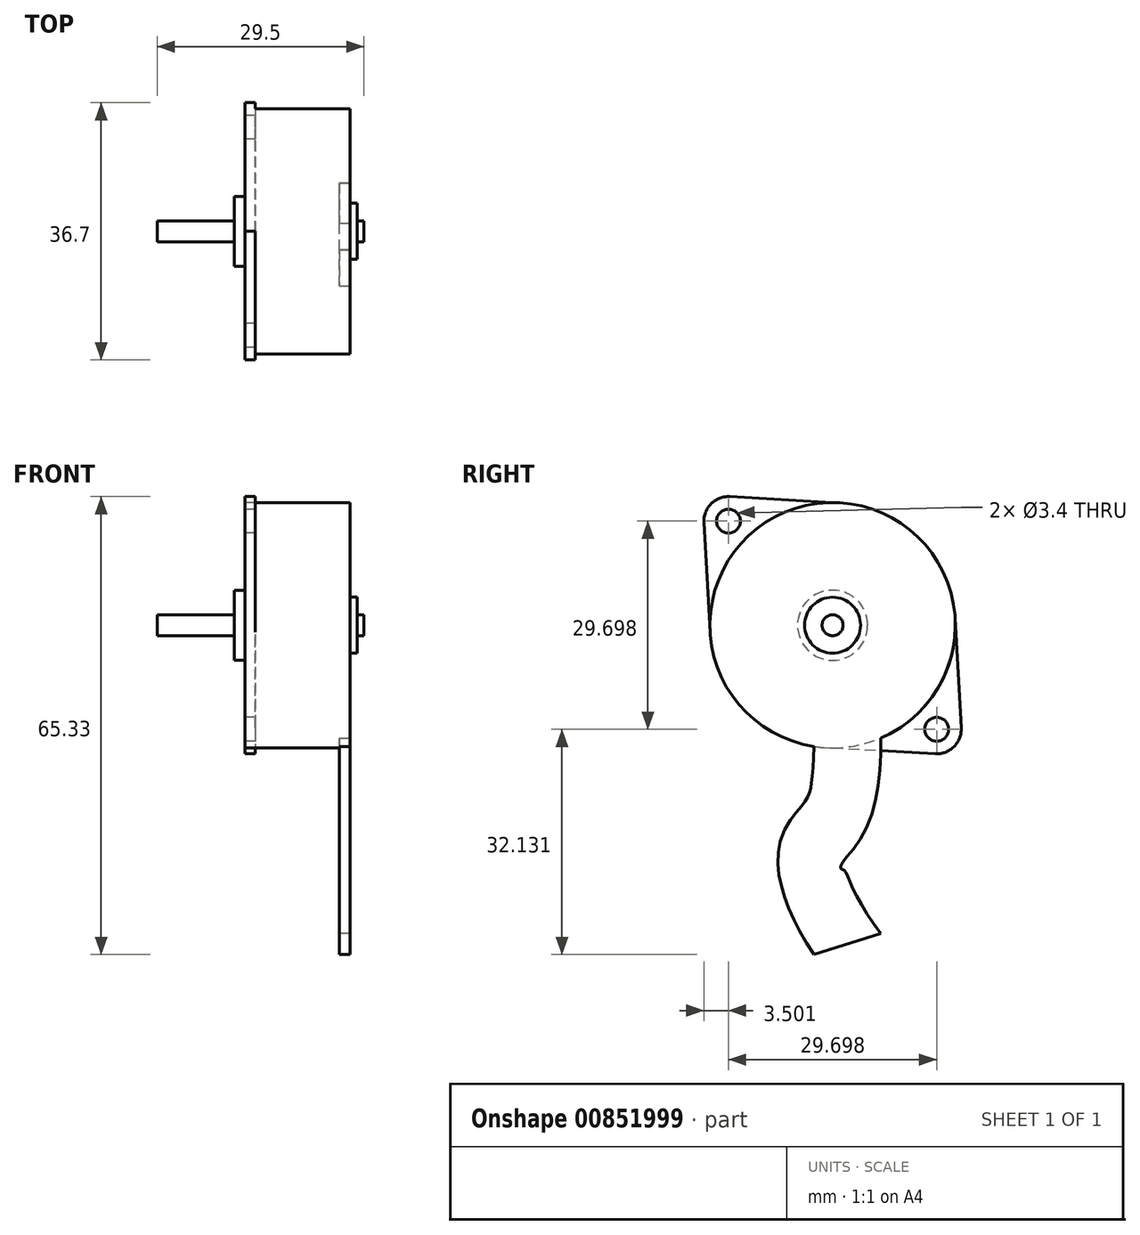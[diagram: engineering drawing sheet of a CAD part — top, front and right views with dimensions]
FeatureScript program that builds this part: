
annotation { "Feature Type Name" : "Feature", "Feature Type Description" : "" }
export const myFeature = defineFeature(function(context is Context, id is Id, definition is map)
    precondition{}
    {
        {
            var Q0;
            Q0=qCreatedBy(makeId("Front.planeOp"),FACE);
            var sketch = newSketch(context, id + "F0", { "sketchPlane" : qUnion([Q0])});
            skLineSegment(sketch, "E0", {"start": v(0, 17.5) * mm, "end": v(15, 17.5) * mm});
            skLineSegment(sketch, "E1", {"start": v(17, 0) * mm, "end": v(0, 0) * mm});
            skLineSegment(sketch, "E2", {"start": v(15, 4) * mm, "end": v(16, 4) * mm});
            skLineSegment(sketch, "E3", {"start": v(16, 4) * mm, "end": v(16, 1.5) * mm});
            skLineSegment(sketch, "E4", {"start": v(16, 1.5) * mm, "end": v(17, 1.5) * mm});
            skLineSegment(sketch, "E5", {"start": v(17, 1.5) * mm, "end": v(17, 0) * mm});
            skLineSegment(sketch, "E6", {"start": v(15, 17.5) * mm, "end": v(15, 4) * mm});
            skLineSegment(sketch, "E7", {"start": v(0, 17.5) * mm, "end": v(0, 5) * mm});
            skLineSegment(sketch, "E8", {"start": v(0, 5) * mm, "end": v(-1.5, 5) * mm});
            skLineSegment(sketch, "E9", {"start": v(-1.5, 5) * mm, "end": v(-1.5, 1.5) * mm});
            skLineSegment(sketch, "E10", {"start": v(-1.5, 1.5) * mm, "end": v(-12.5, 1.5) * mm});
            skLineSegment(sketch, "E11", {"start": v(-12.5, 1.5) * mm, "end": v(-12.5, 0) * mm});
            skLineSegment(sketch, "E12", {"start": v(-12.5, 0) * mm, "end": v(0, 0) * mm});
            skSolve(sketch);
        }
        {
            var Q0;
            Q0=qCreatedBy(makeId("Front.planeOp"),FACE);
            var sketch = newSketch(context, id + "F1", { "sketchPlane" : qUnion([Q0])});
            skLineSegment(sketch, "E13", {"start": v(26.37, 0) * mm, "end": v(-33.57, 0) * mm, "construction": true});
            skSolve(sketch);
        }
        {
            var Q0;
            Q0 = qSketchRegion(id + "F0", true);
            var Q1;
            Q1 = qConstructionFilter(qBodyType(qCreatedBy(id + "F0" ,EDGE), BodyType.WIRE), ConstructionObject.NO);
            var Q2;
            Q2=sQuery(id+"F1.wireOp",EDGE,"E13");
            revolve(context, id + "F2", {"surfaceOperationType" : NewSurfaceOperationType.ADD, "entities" : qUnion([Q0]), "surfaceEntities" : qUnion([Q1]), "axis" : qUnion([Q2]), "revolveType" : RevolveType.FULL});
        }
        {
            var Q0;
            Q0=makeQuery(id+"F2.opRevolve","SWEPT_FACE",FACE,{"disambiguationData":[OSD([sQuery(id+"F0.wireOp",EDGE,"E7")])]});
            var sketch = newSketch(context, id + "F3", { "sketchPlane" : qUnion([Q0])});
            skLineSegment(sketch, "E14", {"start": v(0, -17.5) * mm, "end": v(-14.65, -18.34) * mm});
            skLineSegment(sketch, "E15", {"start": v(-18.34, -14.65) * mm, "end": v(-17.47, 0.97) * mm});
            skLineSegment(sketch, "E16", {"start": v(17.47, -0.97) * mm, "end": v(18.34, 14.65) * mm});
            skLineSegment(sketch, "E17", {"start": v(14.65, 18.34) * mm, "end": v(0, 17.5) * mm});
            skPoint(sketch, "E18.visualSharp", {"position": v(-18.56, -18.57) * mm});
            skArc(sketch, "E18.filletArc", {"start": v(-18.34, -14.65) * mm, "mid": v(-17.32, -17.33) * mm, "end": v(-14.65, -18.34) * mm});
            skPoint(sketch, "E19.visualSharp", {"position": v(18.56, 18.57) * mm});
            skArc(sketch, "E19.filletArc", {"start": v(18.34, 14.65) * mm, "mid": v(17.32, 17.33) * mm, "end": v(14.65, 18.34) * mm});
            skCircle(sketch, "E20", {"center": v(-14.85, -14.85) * mm, "radius": 1.7 * mm});
            skCircle(sketch, "E21", {"center": v(14.85, 14.85) * mm, "radius": 1.7 * mm});
            skLineSegment(sketch, "E22", {"start": v(-14.85, -14.85) * mm, "end": v(14.85, 14.85) * mm, "construction": true});
            skLineSegment(sketch, "E23", {"start": v(0, 17.5) * mm, "end": v(0, -17.5) * mm, "construction": true});
            skArc(sketch, "E24.0", {"start": v(0, -17.5) * mm, "mid": v(12.03, -12.71) * mm, "end": v(17.47, -0.97) * mm});
            skArc(sketch, "E25.trimOffspring", {"start": v(0, 17.5) * mm, "mid": v(-12.03, 12.71) * mm, "end": v(-17.47, 0.97) * mm});
            skSolve(sketch);
        }
        {
            var Q0;
            Q0 = qSketchRegion(id + "F3", true);
            extrude(context, id + "F4", {"entities" : qUnion([Q0]), "operationType" : NewBodyOperationType.ADD, "oppositeDirection" : true, "depth" : 1.5 * mm, "offsetDistance" : 25 * mm});
        }
        {
            var Q0;
            Q0=makeQuery(id+"F2.opRevolve","SWEPT_FACE",FACE,{"disambiguationData":[OSD([sQuery(id+"F0.wireOp",EDGE,"E6")])]});
            var sketch = newSketch(context, id + "F5", { "sketchPlane" : qUnion([Q0])});
            skFitSpline(sketch, "E26", {"points": [v(0, 0) * mm, v(0.99, -25.6) * mm, v(-2.76, -32.07) * mm, v(2.1, -45.5) * mm], "startDerivative": vector(13.26, -42.1) * mm, "endDerivative": vector(35.28, -50.9) * mm});
            skSolve(sketch);
        }
        {
            var Q0;
            Q0=qCreatedBy(makeId("Top.planeOp"),FACE);
            var sketch = newSketch(context, id + "F6", { "sketchPlane" : qUnion([Q0])});
            skLineSegment(sketch, "E27.bottom", {"start": v(15, -5) * mm, "end": v(13.5, -5) * mm});
            skLineSegment(sketch, "E27.top", {"start": v(15, 5) * mm, "end": v(13.5, 5) * mm});
            skLineSegment(sketch, "E27.left", {"start": v(15, -5) * mm, "end": v(15, 5) * mm});
            skLineSegment(sketch, "E27.right", {"start": v(13.5, -5) * mm, "end": v(13.5, 5) * mm});
            skSolve(sketch);
        }
        {
            var Q0;
            Q0 = qSketchRegion(id + "F6", true);
            var Q1;
            Q1 = qConstructionFilter(qBodyType(qCreatedBy(id + "F5" ,EDGE), BodyType.WIRE), ConstructionObject.NO);
            sweep(context, id + "F7", {"operationType" : NewBodyOperationType.ADD, "profiles" : qUnion([Q0]), "path" : qUnion([Q1])});
        }
    });
